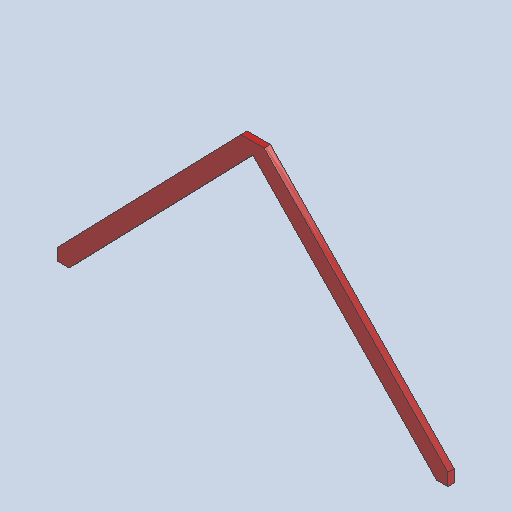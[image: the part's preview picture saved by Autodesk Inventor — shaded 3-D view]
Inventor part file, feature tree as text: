
AUTODESK INVENTOR PART (.ipt)
format: ipt  version: 2025 (Build 290162000, 162)  size: 97,280 bytes
history: native  units: in
note: dims shown in document units (in); Inventor stores cm internally (conversion verified against a paired STEP export)
features: other x7, reference x4, extrude x1, sketch x1
ambient origin geometry x8: Origin, YZ Plane, XZ Plane, XY Plane, X Axis, Y Axis, Z Axis, Center Point
bodies: Solid1 (feature_tree)
feature tree (13):
  extrude  "Extrusion1"  [1 undecoded]
  sketch  "Sketch1"  dims[d0=1.5in d1=0.0in]
  reference  "Reference1"
  reference  "Reference2"
  reference  "Reference3"
  reference  "Reference4"
  other  "<userpath>\Documents\USCTigerBurn24\Tburn24\Legs0\B_Legs0.iam"
  other  "B_Legs0.iam"
  other  "8'x2x4:4"
  other  "4x2x4:3"
  other  "8'x2x4:2"
  other  "4x2x4:2"
  other  "Finish1"
note: 1 required parameter value undecoded (feature->parameter linkage not recoverable at this tier; creation-order binding heuristic only, values carry confidence <= 0.55)
